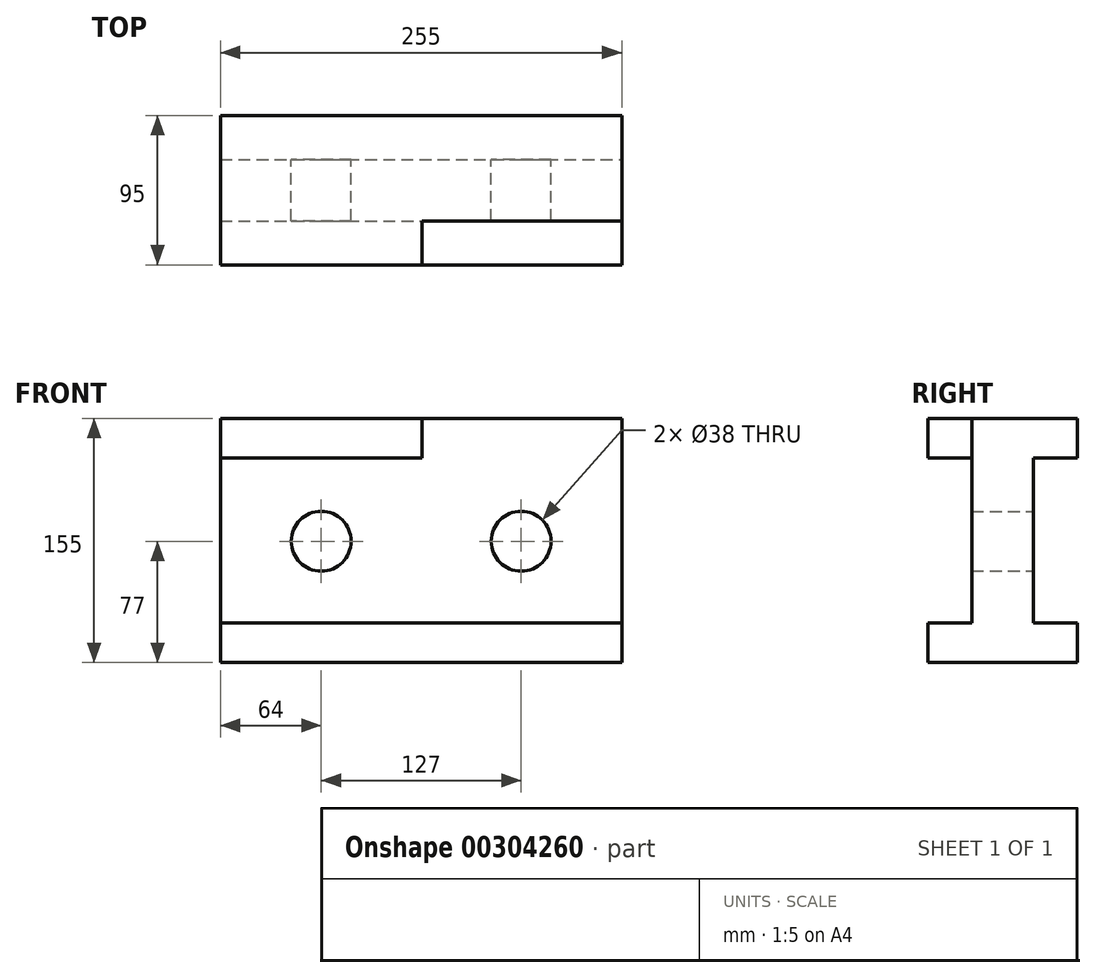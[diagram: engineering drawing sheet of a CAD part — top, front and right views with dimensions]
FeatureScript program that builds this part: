
annotation { "Feature Type Name" : "Feature", "Feature Type Description" : "" }
export const myFeature = defineFeature(function(context is Context, id is Id, definition is map)
    precondition{}
    {
        {
            var Q0;
            Q0=qCreatedBy(makeId("Front.planeOp"),FACE);
            var sketch = newSketch(context, id + "F0", { "sketchPlane" : qUnion([Q0])});
            skLineSegment(sketch, "E0.bottom", {"start": v(0, 0) * mm, "end": v(255, 0) * mm});
            skLineSegment(sketch, "E0.top", {"start": v(0, 155) * mm, "end": v(255, 155) * mm});
            skLineSegment(sketch, "E0.left", {"start": v(0, 0) * mm, "end": v(0, 155) * mm});
            skLineSegment(sketch, "E0.right", {"start": v(255, 0) * mm, "end": v(255, 155) * mm});
            skCircle(sketch, "E1", {"center": v(64, 77) * mm, "radius": 19 * mm});
            skCircle(sketch, "E2", {"center": v(191, 77) * mm, "radius": 19 * mm});
            skSolve(sketch);
        }
        {
            var Q0;
            Q0=makeQuery(id+"F0.imprint","IMPRINT",FACE,{"disambiguationData":[TD([[makeQuery(id+"F0.imprint","IMPRINT",EDGE,{"derivedFrom":sQuery(id+"F0.wireOp",EDGE,"E0.bottom")}),1.0]])]});
            extrude(context, id + "F1", {"entities" : qUnion([Q0]), "depth" : 95 * mm});
        }
        {
            var Q0;
            Q0=makeQuery(id+"F1.opExtrude","CAP_FACE",FACE,{"disambiguationData":[OSD([sQuery(id+"F0.wireOp",EDGE,"E0.bottom"),sQuery(id+"F0.wireOp",EDGE,"E0.top"),sQuery(id+"F0.wireOp",EDGE,"E0.left"),sQuery(id+"F0.wireOp",EDGE,"E0.right"),sQuery(id+"F0.wireOp",EDGE,"E1"),sQuery(id+"F0.wireOp",EDGE,"E2")])],"isStart":false});
            var sketch = newSketch(context, id + "F2", { "sketchPlane" : qUnion([Q0])});
            skLineSegment(sketch, "E3.bottom", {"start": v(-50, 130) * mm, "end": v(305, 130) * mm});
            skLineSegment(sketch, "E3.top", {"start": v(-50, 25) * mm, "end": v(305, 25) * mm});
            skLineSegment(sketch, "E3.left", {"start": v(-50, 130) * mm, "end": v(-50, 25) * mm});
            skLineSegment(sketch, "E3.right", {"start": v(305, 130) * mm, "end": v(305, 25) * mm});
            skLineSegment(sketch, "E4.bottom", {"start": v(305, 130) * mm, "end": v(128, 130) * mm});
            skLineSegment(sketch, "E4.top", {"start": v(305, 190.76) * mm, "end": v(128, 190.76) * mm});
            skLineSegment(sketch, "E4.left", {"start": v(305, 130) * mm, "end": v(305, 190.76) * mm});
            skLineSegment(sketch, "E4.right", {"start": v(128, 130) * mm, "end": v(128, 190.76) * mm});
            skSolve(sketch);
        }
        {
            var Q0;
            Q0=makeQuery(id+"F2.imprint","IMPRINT",FACE,{"disambiguationData":[TD([[makeQuery(id+"F2.imprint","IMPRINT",EDGE,{"derivedFrom":makeQuery(id+"F1.opExtrude","CAP_EDGE",EDGE,{"disambiguationData":[OSD([sQuery(id+"F0.wireOp",EDGE,"E1")])],"isStart":false})}),-1.0]])]});
            var Q1;
            {var subQ0=sQuery(id+"F2.wireOp",EDGE,"E3.left");Q1=makeQuery(id+"F2.imprint","IMPRINT",FACE,{"disambiguationData":[TD([[makeQuery(id+"F2.imprint","IMPRINT",EDGE,{"derivedFrom":subQ0}),1.0]])]});}
            var Q2;
            {var subQ0=sQuery(id+"F2.wireOp",EDGE,"E3.right");Q2=makeQuery(id+"F2.imprint","IMPRINT",FACE,{"disambiguationData":[TD([[makeQuery(id+"F2.imprint","IMPRINT",EDGE,{"derivedFrom":subQ0}),-1.0]])]});}
            var Q3;
            {var subQ1=sQuery(id+"F2.wireOp",EDGE,"E4.top");Q3=makeQuery(id+"F2.imprint","IMPRINT",FACE,{"disambiguationData":[TD([[makeQuery(id+"F2.imprint","IMPRINT",EDGE,{"derivedFrom":subQ1}),1.0]])]});}
            var Q4;
            {var subQ3=makeQuery(id+"F1.opExtrude","CAP_EDGE",EDGE,{"disambiguationData":[OSD([sQuery(id+"F0.wireOp",EDGE,"E0.right")])],"isStart":false});var subQ5=makeQuery(id+"F1.opExtrude","CAP_EDGE",EDGE,{"disambiguationData":[OSD([sQuery(id+"F0.wireOp",EDGE,"E0.top")])],"isStart":false});var subQ7=makeQuery(id+"F2.imprint","INTERSECT",VERTEX,{"derivedFrom":[subQ5,subQ3]});Q4=makeQuery(id+"F2.imprint","IMPRINT",FACE,{"disambiguationData":[TD([[makeQuery(id+"F2.imprint","IMPRINT",EDGE,{"disambiguationData":[TD([[subQ7,1.0]])],"derivedFrom":subQ5}),-1.0]])]});}
            extrude(context, id + "F3", {"entities" : qUnion([Q0, Q1, Q2, Q3, Q4]), "operationType" : NewBodyOperationType.REMOVE, "oppositeDirection" : true, "depth" : 28 * mm});
        }
        {
            var Q0;
            Q0=makeQuery(id+"F1.opExtrude","SWEPT_FACE",FACE,{"disambiguationData":[OSD([sQuery(id+"F0.wireOp",EDGE,"E0.right")])]});
            var sketch = newSketch(context, id + "F4", { "sketchPlane" : qUnion([Q0])});
            skLineSegment(sketch, "E5.bottom", {"start": v(41.41, 130) * mm, "end": v(-28, 130) * mm});
            skLineSegment(sketch, "E5.top", {"start": v(41.41, 25) * mm, "end": v(-28, 25) * mm});
            skLineSegment(sketch, "E5.left", {"start": v(41.41, 130) * mm, "end": v(41.41, 25) * mm});
            skLineSegment(sketch, "E5.right", {"start": v(-28, 130) * mm, "end": v(-28, 25) * mm});
            skSolve(sketch);
        }
        {
            var Q0;
            {var subQ0=sQuery(id+"F4.wireOp",EDGE,"E5.left");Q0=makeQuery(id+"F4.imprint","IMPRINT",FACE,{"disambiguationData":[TD([[makeQuery(id+"F4.imprint","IMPRINT",EDGE,{"derivedFrom":subQ0}),-1.0]])]});}
            var Q1;
            {var subQ0=sQuery(id+"F4.wireOp",EDGE,"E5.right");Q1=makeQuery(id+"F4.imprint","IMPRINT",FACE,{"disambiguationData":[TD([[makeQuery(id+"F4.imprint","IMPRINT",EDGE,{"derivedFrom":subQ0}),1.0]])]});}
            extrude(context, id + "F5", {"entities" : qUnion([Q0, Q1]), "operationType" : NewBodyOperationType.REMOVE, "endBound" : BoundingType.THROUGH_ALL, "oppositeDirection" : true, "depth" : 25 * mm});
        }
    });
